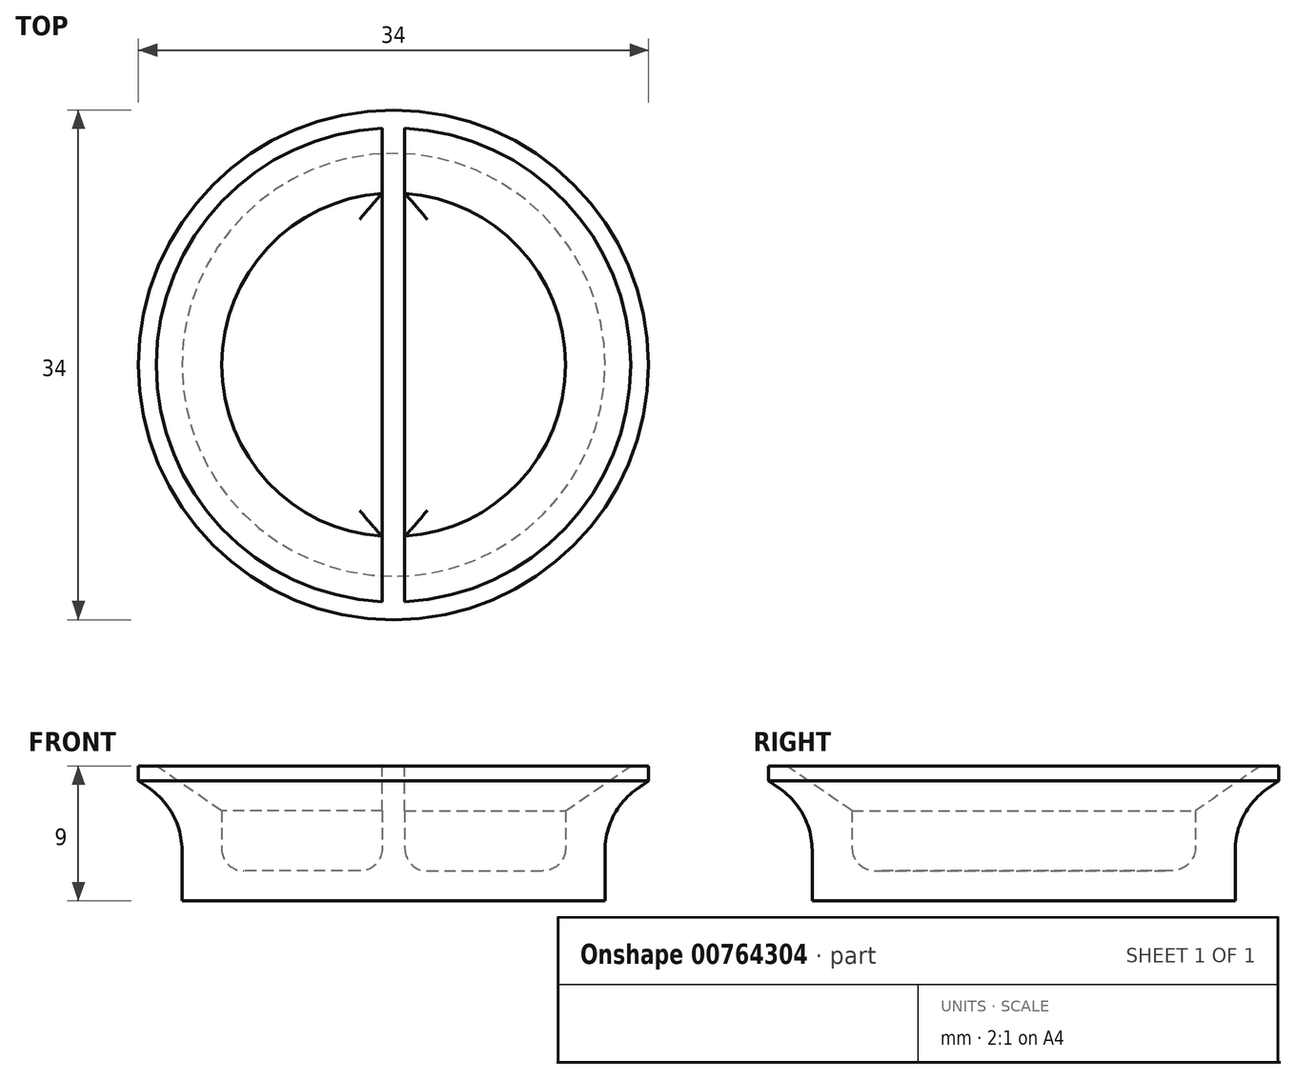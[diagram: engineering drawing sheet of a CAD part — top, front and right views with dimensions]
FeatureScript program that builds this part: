
annotation { "Feature Type Name" : "Feature", "Feature Type Description" : "" }
export const myFeature = defineFeature(function(context is Context, id is Id, definition is map)
    precondition{}
    {
        {
            var Q0;
            Q0=qCreatedBy(makeId("Front.planeOp"),FACE);
            var sketch = newSketch(context, id + "F0", { "sketchPlane" : qUnion([Q0])});
            skLineSegment(sketch, "E0", {"start": v(0, 0) * mm, "end": v(0, 9) * mm});
            skLineSegment(sketch, "E1", {"start": v(0, 9) * mm, "end": v(17, 9) * mm});
            skLineSegment(sketch, "E2", {"start": v(17, 9) * mm, "end": v(17, 8) * mm});
            skLineSegment(sketch, "E3", {"start": v(17, 8) * mm, "end": v(14.1, 6) * mm});
            skLineSegment(sketch, "E4", {"start": v(14.1, 6) * mm, "end": v(14.1, 0) * mm});
            skLineSegment(sketch, "E5", {"start": v(14.1, 0) * mm, "end": v(0, 0) * mm});
            skLineSegment(sketch, "E6", {"start": v(0, 2) * mm, "end": v(11.46, 2) * mm});
            skLineSegment(sketch, "E7", {"start": v(11.46, 2) * mm, "end": v(11.46, 6) * mm});
            skLineSegment(sketch, "E8", {"start": v(11.46, 6) * mm, "end": v(15.8, 9) * mm});
            skSolve(sketch);
        }
        {
            var Q0;
            {var subQ0=sQuery(id+"F0.wireOp",EDGE,"E2");Q0=makeQuery(id+"F0.imprint","IMPRINT",FACE,{"disambiguationData":[TD([[makeQuery(id+"F0.imprint","IMPRINT",EDGE,{"derivedFrom":subQ0}),-1.0]])]});}
            var Q1;
            Q1=sQuery(id+"F0.wireOp",EDGE,"E0");
            revolve(context, id + "F1", {"surfaceOperationType" : NewSurfaceOperationType.NEW, "entities" : qUnion([Q0]), "axis" : qUnion([Q1]), "revolveType" : RevolveType.FULL});
        }
        {
            var Q0;
            Q0=qCreatedBy(makeId("Right.planeOp"),FACE);
            var sketch = newSketch(context, id + "F2", { "sketchPlane" : qUnion([Q0])});
            skLineSegment(sketch, "E9", {"start": v(14.1, 6) * mm, "end": v(14.1, 0) * mm});
            skLineSegment(sketch, "E10", {"start": v(-14.1, 0) * mm, "end": v(-14.1, 6) * mm});
            skLineSegment(sketch, "E11", {"start": v(-14.1, 6) * mm, "end": v(-17, 8) * mm});
            skLineSegment(sketch, "E12", {"start": v(17, 8) * mm, "end": v(14.1, 6) * mm});
            skLineSegment(sketch, "E13", {"start": v(17, 9) * mm, "end": v(17, 8) * mm});
            skLineSegment(sketch, "E14", {"start": v(-17, 8) * mm, "end": v(-17, 9) * mm});
            skLineSegment(sketch, "E15", {"start": v(-16, 9) * mm, "end": v(-16, 8) * mm});
            skLineSegment(sketch, "E16", {"start": v(-16, 8) * mm, "end": v(-13.1, 6) * mm});
            skLineSegment(sketch, "E17", {"start": v(-13.1, 6) * mm, "end": v(-13.1, 0) * mm});
            skLineSegment(sketch, "E18", {"start": v(-13.1, 0) * mm, "end": v(13.1, 0) * mm});
            skLineSegment(sketch, "E19", {"start": v(13.1, 0) * mm, "end": v(13.1, 6) * mm});
            skLineSegment(sketch, "E20", {"start": v(13.1, 6) * mm, "end": v(16, 8) * mm});
            skLineSegment(sketch, "E21", {"start": v(16, 8) * mm, "end": v(16, 9) * mm});
            skLineSegment(sketch, "E22", {"start": v(16, 9) * mm, "end": v(-16, 9) * mm});
            skLineSegment(sketch, "E23", {"start": v(-14.1, 6) * mm, "end": v(-13.1, 6) * mm, "construction": true});
            skLineSegment(sketch, "E24", {"start": v(-17, 8) * mm, "end": v(-16, 8) * mm, "construction": true});
            skLineSegment(sketch, "E25", {"start": v(0, 9) * mm, "end": v(0, 0) * mm, "construction": true});
            skLineSegment(sketch, "E26", {"start": v(13.1, 6) * mm, "end": v(14.1, 6) * mm, "construction": true});
            skLineSegment(sketch, "E27", {"start": v(16, 8) * mm, "end": v(17, 8) * mm, "construction": true});
            skSolve(sketch);
        }
        {
            var Q0;
            Q0 = qSketchRegion(id + "F2", true);
            extrude(context, id + "F3", {"entities" : qUnion([Q0]), "operationType" : NewBodyOperationType.ADD, "endBound" : BoundingType.SYMMETRIC, "depth" : 1.5 * mm, "offsetDistance" : 25 * mm});
        }
        {
            var Q0;
            {var subQ0=sQuery(id+"F0.wireOp",EDGE,"E6");var subQ1=sQuery(id+"F0.wireOp",EDGE,"E7");Q0=makeQuery(id+"F3.boolean.opBoolean","SPLIT",EDGE,{"disambiguationData":[TD([makeQuery(id+"F3.opExtrude","CAP_FACE",FACE,{"disambiguationData":[OSD([sQuery(id+"F2.wireOp",EDGE,"E15"),sQuery(id+"F2.wireOp",EDGE,"E16"),sQuery(id+"F2.wireOp",EDGE,"E17"),sQuery(id+"F2.wireOp",EDGE,"E18"),sQuery(id+"F2.wireOp",EDGE,"E19"),sQuery(id+"F2.wireOp",EDGE,"E20"),sQuery(id+"F2.wireOp",EDGE,"E21"),sQuery(id+"F2.wireOp",EDGE,"E22")])],"isStart":true})])],"derivedFrom":makeQuery(id+"F1.opRevolve","SWEPT_EDGE",EDGE,{"disambiguationData":[OSD([subQ0,subQ1])]})});}
            var Q1;
            Q1=makeQuery(id+"F3.boolean.opBoolean","INTERSECT",EDGE,{"derivedFrom":[makeQuery(id+"F1.opRevolve","SWEPT_FACE",FACE,{"disambiguationData":[OSD([sQuery(id+"F0.wireOp",EDGE,"E6")])]}),makeQuery(id+"F3.opExtrude","CAP_FACE",FACE,{"disambiguationData":[OSD([sQuery(id+"F2.wireOp",EDGE,"E15"),sQuery(id+"F2.wireOp",EDGE,"E16"),sQuery(id+"F2.wireOp",EDGE,"E17"),sQuery(id+"F2.wireOp",EDGE,"E18"),sQuery(id+"F2.wireOp",EDGE,"E19"),sQuery(id+"F2.wireOp",EDGE,"E20"),sQuery(id+"F2.wireOp",EDGE,"E21"),sQuery(id+"F2.wireOp",EDGE,"E22")])],"isStart":false})]});
            var Q2;
            {var subQ0=sQuery(id+"F0.wireOp",EDGE,"E6");var subQ1=sQuery(id+"F0.wireOp",EDGE,"E7");Q2=makeQuery(id+"F3.boolean.opBoolean","SPLIT",EDGE,{"disambiguationData":[TD([makeQuery(id+"F3.opExtrude","CAP_FACE",FACE,{"disambiguationData":[OSD([sQuery(id+"F2.wireOp",EDGE,"E15"),sQuery(id+"F2.wireOp",EDGE,"E16"),sQuery(id+"F2.wireOp",EDGE,"E17"),sQuery(id+"F2.wireOp",EDGE,"E18"),sQuery(id+"F2.wireOp",EDGE,"E19"),sQuery(id+"F2.wireOp",EDGE,"E20"),sQuery(id+"F2.wireOp",EDGE,"E21"),sQuery(id+"F2.wireOp",EDGE,"E22")])],"isStart":false})])],"derivedFrom":makeQuery(id+"F1.opRevolve","SWEPT_EDGE",EDGE,{"disambiguationData":[OSD([subQ0,subQ1])]})});}
            var Q3;
            Q3=makeQuery(id+"F3.boolean.opBoolean","INTERSECT",EDGE,{"derivedFrom":[makeQuery(id+"F1.opRevolve","SWEPT_FACE",FACE,{"disambiguationData":[OSD([sQuery(id+"F0.wireOp",EDGE,"E6")])]}),makeQuery(id+"F3.opExtrude","CAP_FACE",FACE,{"disambiguationData":[OSD([sQuery(id+"F2.wireOp",EDGE,"E15"),sQuery(id+"F2.wireOp",EDGE,"E16"),sQuery(id+"F2.wireOp",EDGE,"E17"),sQuery(id+"F2.wireOp",EDGE,"E18"),sQuery(id+"F2.wireOp",EDGE,"E19"),sQuery(id+"F2.wireOp",EDGE,"E20"),sQuery(id+"F2.wireOp",EDGE,"E21"),sQuery(id+"F2.wireOp",EDGE,"E22")])],"isStart":true})]});
            fillet(context, id + "F4", {"entities" : qUnion([Q0, Q1, Q2, Q3]), "radius" : 1.5 * mm, "tangentPropagation" : true, "allowEdgeOverflow" : false});
        }
        {
            var Q0;
            Q0=makeQuery(id+"F1.opRevolve","SWEPT_EDGE",EDGE,{"disambiguationData":[OSD([sQuery(id+"F0.wireOp",EDGE,"E3"),sQuery(id+"F0.wireOp",EDGE,"E4")])]});
            fillet(context, id + "F5", {"entities" : qUnion([Q0]), "radius" : 5 * mm, "tangentPropagation" : true, "allowEdgeOverflow" : false});
        }
    });
